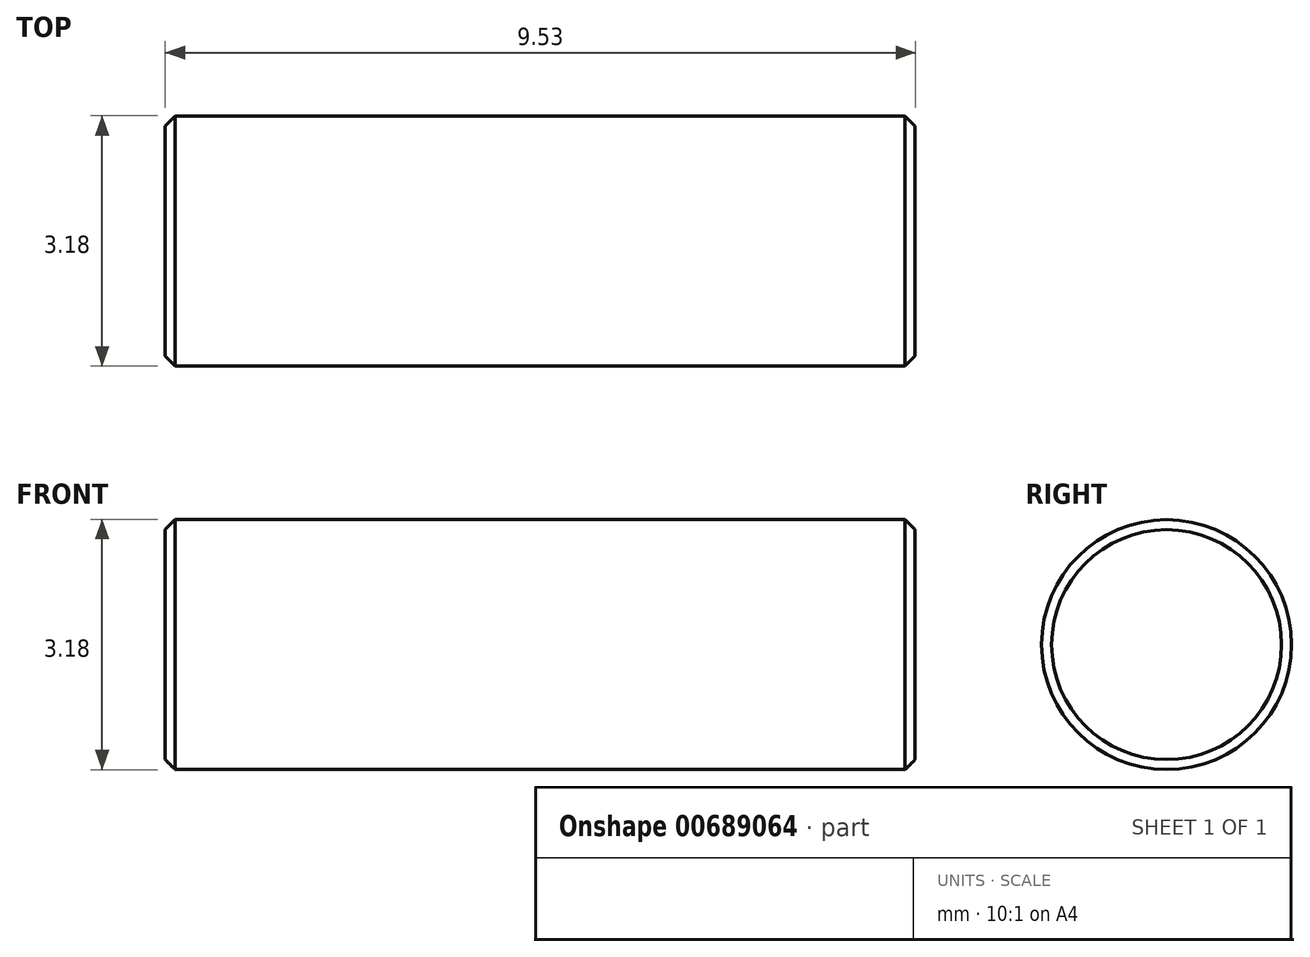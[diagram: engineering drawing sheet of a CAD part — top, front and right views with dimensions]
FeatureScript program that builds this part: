
annotation { "Feature Type Name" : "Feature", "Feature Type Description" : "" }
export const myFeature = defineFeature(function(context is Context, id is Id, definition is map)
    precondition{}
    {
        {
            var Q0;
            Q0=qCreatedBy(makeId("Right.planeOp"),FACE);
            var sketch = newSketch(context, id + "F0", { "sketchPlane" : qUnion([Q0])});
            skCircle(sketch, "E0", {"center": v(0, 0) * mm, "radius": 1.59 * mm});
            skSolve(sketch);
        }
        {
            var Q0;
            Q0=makeQuery(id+"F0.imprint","IMPRINT",FACE,{"disambiguationData":[TD([[makeQuery(id+"F0.imprint","IMPRINT",EDGE,{"derivedFrom":sQuery(id+"F0.wireOp",EDGE,"E0")}),1.0]])]});
            extrude(context, id + "F1", {"entities" : qUnion([Q0]), "depth" : 9.52 * mm, "offsetDistance" : 25.4 * mm});
        }
        {
            var Q0;
            Q0=makeQuery(id+"F1.opExtrude","CAP_EDGE",EDGE,{"disambiguationData":[OSD([sQuery(id+"F0.wireOp",EDGE,"E0")])],"isStart":false});
            chamfer(context, id + "F2", {"entities" : qUnion([Q0]), "width" : 0.13 * mm, "tangentPropagation" : true});
        }
        {
            var Q0;
            Q0=makeQuery(id+"F1.opExtrude","CAP_EDGE",EDGE,{"disambiguationData":[OSD([sQuery(id+"F0.wireOp",EDGE,"E0")])],"isStart":true});
            chamfer(context, id + "F3", {"entities" : qUnion([Q0]), "width" : 0.13 * mm, "tangentPropagation" : true});
        }
    });
